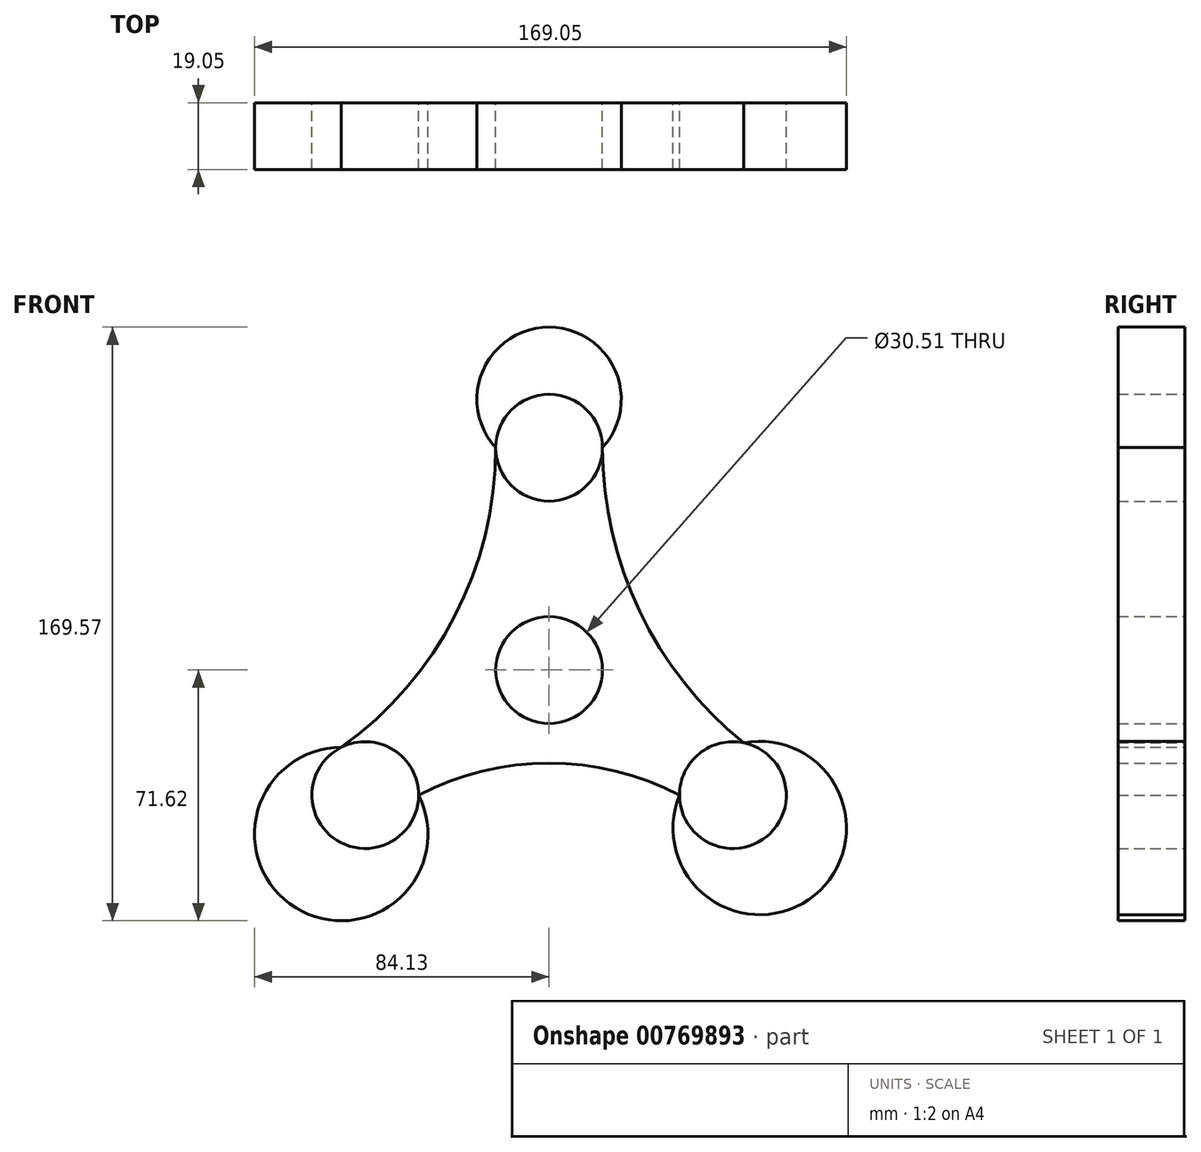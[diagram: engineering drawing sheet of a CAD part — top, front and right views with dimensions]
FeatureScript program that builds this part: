
annotation { "Feature Type Name" : "Feature", "Feature Type Description" : "" }
export const myFeature = defineFeature(function(context is Context, id is Id, definition is map)
    precondition{}
    {
        {
            var Q0;
            Q0=qCreatedBy(makeId("Front.planeOp"),FACE);
            var sketch = newSketch(context, id + "F0", { "sketchPlane" : qUnion([Q0])});
            skCircle(sketch, "E0", {"center": v(0, 0) * mm, "radius": 15.25 * mm});
            skCircle(sketch, "E1", {"center": v(52.5, -35.73) * mm, "radius": 15.25 * mm});
            skCircle(sketch, "E2", {"center": v(-52.5, -35.73) * mm, "radius": 15.25 * mm});
            skCircle(sketch, "E3", {"center": v(0, 63.5) * mm, "radius": 15.25 * mm});
            skArc(sketch, "E4", {"start": v(-59.33, -22.1) * mm, "mid": v(-26.92, 15.36) * mm, "end": v(-15.25, 63.5) * mm});
            skArc(sketch, "E5", {"start": v(15.25, 63.5) * mm, "mid": v(25.86, 16.78) * mm, "end": v(55.6, -20.8) * mm});
            skArc(sketch, "E6", {"start": v(37.24, -35.73) * mm, "mid": v(0, -26.57) * mm, "end": v(-37.24, -35.73) * mm});
            skArc(sketch, "E7", {"start": v(-59.33, -22.1) * mm, "mid": v(-72.37, -67.93) * mm, "end": v(-37.24, -35.73) * mm});
            skArc(sketch, "E8", {"start": v(37.24, -35.73) * mm, "mid": v(75.78, -64.34) * mm, "end": v(55.6, -20.8) * mm});
            skArc(sketch, "E9", {"start": v(15.25, 63.5) * mm, "mid": v(0, 97.95) * mm, "end": v(-15.25, 63.5) * mm});
            skSolve(sketch);
        }
        {
            var Q0;
            Q0=makeQuery(id+"F0.imprint","IMPRINT",FACE,{"disambiguationData":[TD([[makeQuery(id+"F0.imprint","IMPRINT",EDGE,{"derivedFrom":sQuery(id+"F0.wireOp",EDGE,"E0")}),-1.0]])]});
            var Q1;
            {var subQ0=sQuery(id+"F0.wireOp",EDGE,"E9");Q1=makeQuery(id+"F0.imprint","IMPRINT",FACE,{"disambiguationData":[TD([[makeQuery(id+"F0.imprint","IMPRINT",EDGE,{"derivedFrom":subQ0}),1.0]])]});}
            var Q2;
            {var subQ0=sQuery(id+"F0.wireOp",EDGE,"E8");Q2=makeQuery(id+"F0.imprint","IMPRINT",FACE,{"disambiguationData":[TD([[makeQuery(id+"F0.imprint","IMPRINT",EDGE,{"derivedFrom":subQ0}),1.0]])]});}
            var Q3;
            {var subQ0=sQuery(id+"F0.wireOp",EDGE,"E7");Q3=makeQuery(id+"F0.imprint","IMPRINT",FACE,{"disambiguationData":[TD([[makeQuery(id+"F0.imprint","IMPRINT",EDGE,{"derivedFrom":subQ0}),1.0]])]});}
            extrude(context, id + "F1", {"entities" : qUnion([Q0, Q1, Q2, Q3]), "depth" : 19.05 * mm, "offsetDistance" : 25.4 * mm});
        }
    });
